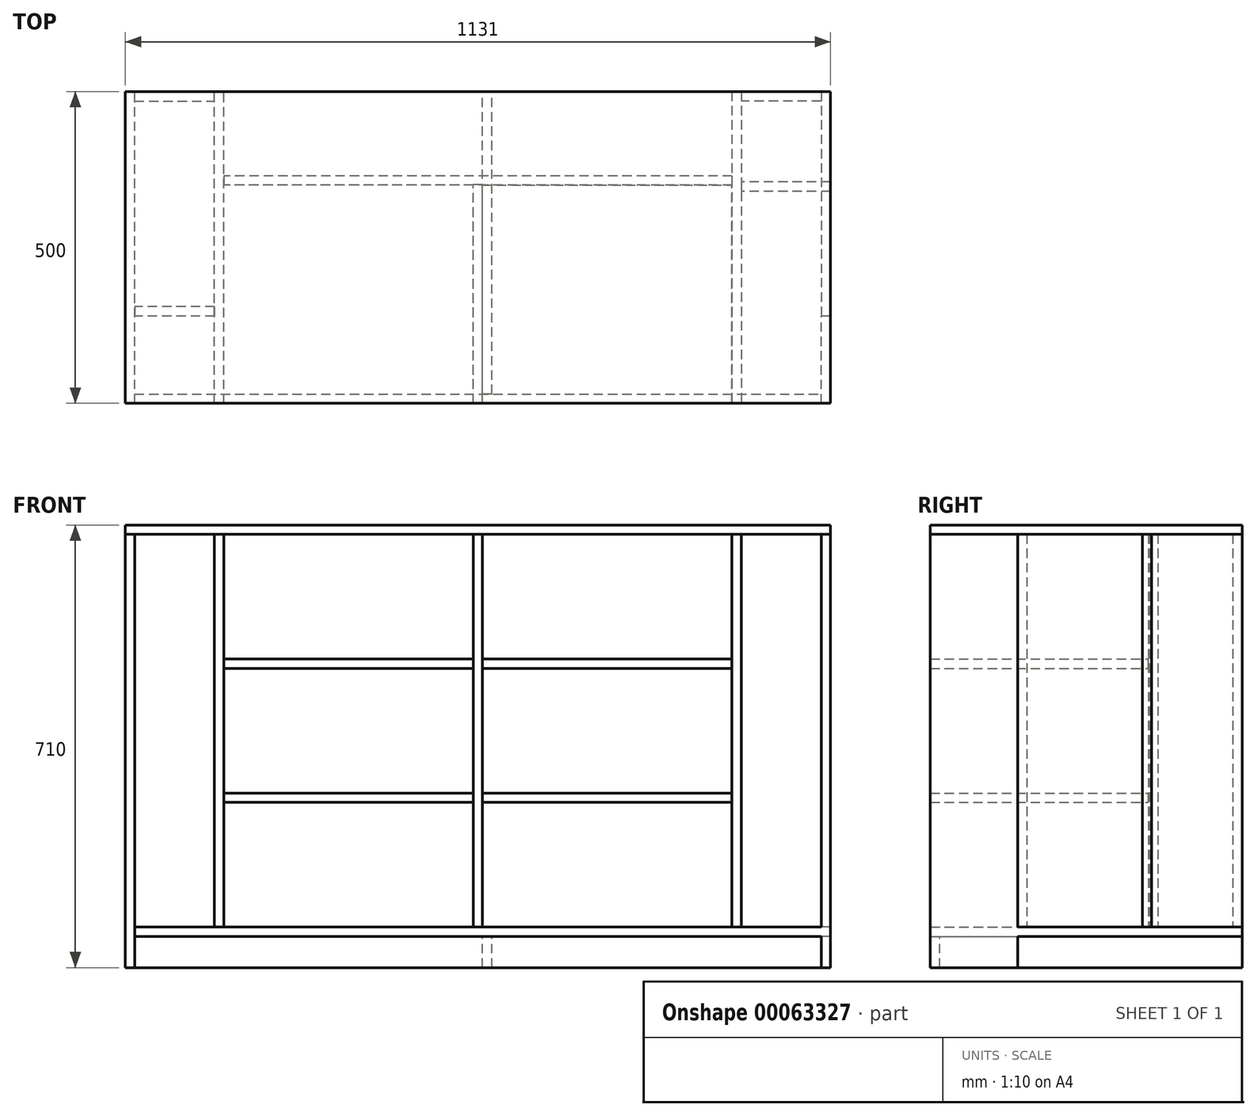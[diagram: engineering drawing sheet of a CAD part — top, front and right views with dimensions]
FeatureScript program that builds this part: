
annotation { "Feature Type Name" : "Feature", "Feature Type Description" : "" }
export const myFeature = defineFeature(function(context is Context, id is Id, definition is map)
    precondition{}
    {
        {
            var Q0;
            Q0=qCreatedBy(makeId("Right.planeOp"),FACE);
            var sketch = newSketch(context, id + "F0", { "sketchPlane" : qUnion([Q0])});
            skLineSegment(sketch, "E0.bottom", {"start": v(0, 0) * mm, "end": v(-500, 0) * mm});
            skLineSegment(sketch, "E0.top", {"start": v(0, 695) * mm, "end": v(-500, 695) * mm});
            skLineSegment(sketch, "E0.left", {"start": v(0, 0) * mm, "end": v(0, 695) * mm});
            skLineSegment(sketch, "E0.right", {"start": v(-500, 0) * mm, "end": v(-500, 695) * mm});
            skSolve(sketch);
        }
        {
            var Q0;
            Q0 = qSketchRegion(id + "F0", true);
            extrude(context, id + "F1", {"entities" : qUnion([Q0]), "depth" : 15 * mm});
        }
        {
            var Q0;
            Q0=makeQuery(id+"F1.opExtrude","SWEPT_FACE",FACE,{"disambiguationData":[OSD([sQuery(id+"F0.wireOp",EDGE,"E0.top")])]});
            var sketch = newSketch(context, id + "F2", { "sketchPlane" : qUnion([Q0])});
            skLineSegment(sketch, "E1.bottom", {"start": v(0, 0) * mm, "end": v(1131, 0) * mm});
            skLineSegment(sketch, "E1.top", {"start": v(0, -500) * mm, "end": v(1131, -500) * mm});
            skLineSegment(sketch, "E1.left", {"start": v(0, 0) * mm, "end": v(0, -500) * mm});
            skLineSegment(sketch, "E1.right", {"start": v(1131, 0) * mm, "end": v(1131, -500) * mm});
            skSolve(sketch);
        }
        {
            var Q0;
            Q0 = qSketchRegion(id + "F2", true);
            extrude(context, id + "F3", {"entities" : qUnion([Q0]), "depth" : 15 * mm});
        }
        {
            var Q0;
            Q0=makeQuery(id+"F1.opExtrude","CAP_FACE",FACE,{"disambiguationData":[OSD([sQuery(id+"F0.wireOp",EDGE,"E0.bottom"),sQuery(id+"F0.wireOp",EDGE,"E0.top"),sQuery(id+"F0.wireOp",EDGE,"E0.left"),sQuery(id+"F0.wireOp",EDGE,"E0.right")])],"isStart":false});
            var sketch = newSketch(context, id + "F4", { "sketchPlane" : qUnion([Q0])});
            skLineSegment(sketch, "E2.bottom", {"start": v(-500, 65) * mm, "end": v(0, 65) * mm});
            skLineSegment(sketch, "E2.top", {"start": v(-500, 50) * mm, "end": v(0, 50) * mm});
            skLineSegment(sketch, "E2.left", {"start": v(-500, 65) * mm, "end": v(-500, 50) * mm});
            skLineSegment(sketch, "E2.right", {"start": v(0, 65) * mm, "end": v(0, 50) * mm});
            skSolve(sketch);
        }
        {
            var Q0;
            Q0 = qSketchRegion(id + "F4", true);
            extrude(context, id + "F5", {"entities" : qUnion([Q0]), "depth" : 1101 * mm});
        }
        {
            var Q0;
            Q0=makeQuery(id+"F5.opExtrude","SWEPT_FACE",FACE,{"disambiguationData":[OSD([sQuery(id+"F4.wireOp",EDGE,"E2.top")])]});
            var sketch = newSketch(context, id + "F6", { "sketchPlane" : qUnion([Q0])});
            skLineSegment(sketch, "E3.bottom", {"start": v(588, 485) * mm, "end": v(573, 485) * mm});
            skLineSegment(sketch, "E3.top", {"start": v(588, 0) * mm, "end": v(573, 0) * mm});
            skLineSegment(sketch, "E3.left", {"start": v(588, 485) * mm, "end": v(588, 0) * mm});
            skLineSegment(sketch, "E3.right", {"start": v(573, 485) * mm, "end": v(573, 0) * mm});
            skSolve(sketch);
        }
        {
            var Q0;
            Q0 = qSketchRegion(id + "F6", true);
            extrude(context, id + "F7", {"entities" : qUnion([Q0]), "depth" : 50 * mm});
        }
        {
            var Q0;
            Q0=makeQuery(id+"F7.opExtrude","SWEPT_FACE",FACE,{"disambiguationData":[OSD([sQuery(id+"F6.wireOp",EDGE,"E3.bottom")])]});
            var sketch = newSketch(context, id + "F8", { "sketchPlane" : qUnion([Q0])});
            skLineSegment(sketch, "E4.bottom", {"start": v(15, 0) * mm, "end": v(1116, 0) * mm});
            skLineSegment(sketch, "E4.top", {"start": v(15, 50) * mm, "end": v(1116, 50) * mm});
            skLineSegment(sketch, "E4.left", {"start": v(15, 0) * mm, "end": v(15, 50) * mm});
            skLineSegment(sketch, "E4.right", {"start": v(1116, 0) * mm, "end": v(1116, 50) * mm});
            skSolve(sketch);
        }
        {
            var Q0;
            Q0 = qSketchRegion(id + "F8", true);
            extrude(context, id + "F9", {"entities" : qUnion([Q0]), "depth" : 15 * mm});
        }
        {
            var Q0;
            Q0=makeQuery(id+"F9.opExtrude","SWEPT_FACE",FACE,{"disambiguationData":[OSD([sQuery(id+"F8.wireOp",EDGE,"E4.right")])]});
            var sketch = newSketch(context, id + "F10", { "sketchPlane" : qUnion([Q0])});
            skLineSegment(sketch, "E5.bottom", {"start": v(-500, 0) * mm, "end": v(-360, 0) * mm});
            skLineSegment(sketch, "E5.top", {"start": v(-500, 695) * mm, "end": v(-360, 695) * mm});
            skLineSegment(sketch, "E5.left", {"start": v(-500, 0) * mm, "end": v(-500, 695) * mm});
            skLineSegment(sketch, "E5.right", {"start": v(-360, 0) * mm, "end": v(-360, 695) * mm});
            skSolve(sketch);
        }
        {
            var Q0;
            Q0 = qSketchRegion(id + "F10", true);
            extrude(context, id + "F11", {"entities" : qUnion([Q0]), "depth" : 15 * mm});
        }
        {
            var Q0;
            Q0=makeQuery(id+"F5.opExtrude","CAP_FACE",FACE,{"disambiguationData":[OSD([sQuery(id+"F4.wireOp",EDGE,"E2.bottom"),sQuery(id+"F4.wireOp",EDGE,"E2.top"),sQuery(id+"F4.wireOp",EDGE,"E2.left"),sQuery(id+"F4.wireOp",EDGE,"E2.right")])],"isStart":false});
            var sketch = newSketch(context, id + "F12", { "sketchPlane" : qUnion([Q0])});
            skLineSegment(sketch, "E6.bottom", {"start": v(0, 65) * mm, "end": v(-360, 65) * mm});
            skLineSegment(sketch, "E6.top", {"start": v(0, 50) * mm, "end": v(-360, 50) * mm});
            skLineSegment(sketch, "E6.left", {"start": v(0, 65) * mm, "end": v(0, 50) * mm});
            skLineSegment(sketch, "E6.right", {"start": v(-360, 65) * mm, "end": v(-360, 50) * mm});
            skSolve(sketch);
        }
        {
            var Q0;
            Q0 = qSketchRegion(id + "F12", true);
            extrude(context, id + "F13", {"entities" : qUnion([Q0]), "operationType" : NewBodyOperationType.ADD, "depth" : 15 * mm});
        }
        {
            var Q0;
            Q0=makeQuery(id+"F13.boolean.opBoolean","MERGE",FACE,{"derivedFrom":[makeQuery(id+"F5.opExtrude","SWEPT_FACE",FACE,{"disambiguationData":[OSD([sQuery(id+"F4.wireOp",EDGE,"E2.top")])]}),makeQuery(id+"F13.opExtrude","SWEPT_FACE",FACE,{"disambiguationData":[OSD([sQuery(id+"F12.wireOp",EDGE,"E6.top")])]})]});
            var sketch = newSketch(context, id + "F14", { "sketchPlane" : qUnion([Q0])});
            skLineSegment(sketch, "E7.bottom", {"start": v(1116, 0) * mm, "end": v(1131, 0) * mm});
            skLineSegment(sketch, "E7.top", {"start": v(1116, 360) * mm, "end": v(1131, 360) * mm});
            skLineSegment(sketch, "E7.left", {"start": v(1116, 0) * mm, "end": v(1116, 360) * mm});
            skLineSegment(sketch, "E7.right", {"start": v(1131, 0) * mm, "end": v(1131, 360) * mm});
            skSolve(sketch);
        }
        {
            var Q0;
            Q0 = qSketchRegion(id + "F14", true);
            extrude(context, id + "F15", {"entities" : qUnion([Q0]), "depth" : 50 * mm});
        }
        {
            var Q0;
            Q0=makeQuery(id+"F3.opExtrude","CAP_FACE",FACE,{"disambiguationData":[OSD([sQuery(id+"F2.wireOp",EDGE,"E1.bottom"),sQuery(id+"F2.wireOp",EDGE,"E1.top"),sQuery(id+"F2.wireOp",EDGE,"E1.left"),sQuery(id+"F2.wireOp",EDGE,"E1.right")])],"isStart":true});
            var sketch = newSketch(context, id + "F16", { "sketchPlane" : qUnion([Q0])});
            skLineSegment(sketch, "E8.bottom", {"start": v(143, 500) * mm, "end": v(158, 500) * mm});
            skLineSegment(sketch, "E8.top", {"start": v(143, 0) * mm, "end": v(158, 0) * mm});
            skLineSegment(sketch, "E8.left", {"start": v(143, 500) * mm, "end": v(143, 0) * mm});
            skLineSegment(sketch, "E8.right", {"start": v(158, 500) * mm, "end": v(158, 0) * mm});
            skSolve(sketch);
        }
        {
            var Q0;
            Q0 = qSketchRegion(id + "F16", true);
            extrude(context, id + "F17", {"entities" : qUnion([Q0]), "depth" : 630 * mm});
        }
        {
            var Q0;
            Q0=makeQuery(id+"F17.opExtrude","SWEPT_FACE",FACE,{"disambiguationData":[OSD([sQuery(id+"F16.wireOp",EDGE,"E8.right")])]});
            var sketch = newSketch(context, id + "F18", { "sketchPlane" : qUnion([Q0])});
            skLineSegment(sketch, "E9.bottom", {"start": v(-500, 480) * mm, "end": v(-150, 480) * mm});
            skLineSegment(sketch, "E9.top", {"start": v(-500, 495) * mm, "end": v(-150, 495) * mm});
            skLineSegment(sketch, "E9.left", {"start": v(-500, 480) * mm, "end": v(-500, 495) * mm});
            skLineSegment(sketch, "E9.right", {"start": v(-150, 480) * mm, "end": v(-150, 495) * mm});
            skSolve(sketch);
        }
        {
            var Q0;
            Q0 = qSketchRegion(id + "F18", true);
            extrude(context, id + "F19", {"entities" : qUnion([Q0]), "depth" : 400 * mm});
        }
        {
            var Q0;
            Q0=makeQuery(id+"F17.opExtrude","SWEPT_FACE",FACE,{"disambiguationData":[OSD([sQuery(id+"F16.wireOp",EDGE,"E8.right")])]});
            var sketch = newSketch(context, id + "F20", { "sketchPlane" : qUnion([Q0])});
            skLineSegment(sketch, "E10.bottom", {"start": v(-500, 265) * mm, "end": v(-150, 265) * mm});
            skLineSegment(sketch, "E10.top", {"start": v(-500, 280) * mm, "end": v(-150, 280) * mm});
            skLineSegment(sketch, "E10.left", {"start": v(-500, 265) * mm, "end": v(-500, 280) * mm});
            skLineSegment(sketch, "E10.right", {"start": v(-150, 265) * mm, "end": v(-150, 280) * mm});
            skSolve(sketch);
        }
        {
            var Q0;
            Q0 = qSketchRegion(id + "F20", true);
            extrude(context, id + "F21", {"entities" : qUnion([Q0]), "depth" : 400 * mm});
        }
        {
            var Q0;
            Q0=makeQuery(id+"F19.opExtrude","SWEPT_FACE",FACE,{"disambiguationData":[OSD([sQuery(id+"F18.wireOp",EDGE,"E9.right")])]});
            var sketch = newSketch(context, id + "F22", { "sketchPlane" : qUnion([Q0])});
            skLineSegment(sketch, "E11.bottom", {"start": v(-973, 695) * mm, "end": v(-158, 695) * mm});
            skLineSegment(sketch, "E11.top", {"start": v(-973, 65) * mm, "end": v(-158, 65) * mm});
            skLineSegment(sketch, "E11.left", {"start": v(-973, 695) * mm, "end": v(-973, 65) * mm});
            skLineSegment(sketch, "E11.right", {"start": v(-158, 695) * mm, "end": v(-158, 65) * mm});
            skSolve(sketch);
        }
        {
            var Q0;
            Q0 = qSketchRegion(id + "F22", true);
            extrude(context, id + "F23", {"entities" : qUnion([Q0]), "depth" : 15 * mm});
        }
        {
            var Q0;
            Q0=makeQuery(id+"F23.opExtrude","SWEPT_FACE",FACE,{"disambiguationData":[OSD([sQuery(id+"F22.wireOp",EDGE,"E11.left")])]});
            var sketch = newSketch(context, id + "F24", { "sketchPlane" : qUnion([Q0])});
            skLineSegment(sketch, "E12.bottom", {"start": v(0, 695) * mm, "end": v(-500, 695) * mm});
            skLineSegment(sketch, "E12.top", {"start": v(0, 65) * mm, "end": v(-500, 65) * mm});
            skLineSegment(sketch, "E12.left", {"start": v(0, 695) * mm, "end": v(0, 65) * mm});
            skLineSegment(sketch, "E12.right", {"start": v(-500, 695) * mm, "end": v(-500, 65) * mm});
            skSolve(sketch);
        }
        {
            var Q0;
            Q0 = qSketchRegion(id + "F24", true);
            extrude(context, id + "F25", {"entities" : qUnion([Q0]), "depth" : 15 * mm});
        }
        {
            var Q0;
            Q0=makeQuery(id+"F23.opExtrude","CAP_FACE",FACE,{"disambiguationData":[OSD([sQuery(id+"F22.wireOp",EDGE,"E11.bottom"),sQuery(id+"F22.wireOp",EDGE,"E11.top"),sQuery(id+"F22.wireOp",EDGE,"E11.left"),sQuery(id+"F22.wireOp",EDGE,"E11.right")])],"isStart":true});
            var sketch = newSketch(context, id + "F26", { "sketchPlane" : qUnion([Q0])});
            skLineSegment(sketch, "E13.bottom", {"start": v(573, 280) * mm, "end": v(973, 280) * mm});
            skLineSegment(sketch, "E13.top", {"start": v(573, 265) * mm, "end": v(973, 265) * mm});
            skLineSegment(sketch, "E13.left", {"start": v(573, 280) * mm, "end": v(573, 265) * mm});
            skLineSegment(sketch, "E13.right", {"start": v(973, 280) * mm, "end": v(973, 265) * mm});
            skSolve(sketch);
        }
        {
            var Q0;
            Q0 = qSketchRegion(id + "F26", true);
            extrude(context, id + "F27", {"entities" : qUnion([Q0]), "depth" : 350 * mm});
        }
        {
            var Q0;
            Q0=makeQuery(id+"F25.opExtrude","CAP_FACE",FACE,{"disambiguationData":[OSD([sQuery(id+"F24.wireOp",EDGE,"E12.bottom"),sQuery(id+"F24.wireOp",EDGE,"E12.top"),sQuery(id+"F24.wireOp",EDGE,"E12.left"),sQuery(id+"F24.wireOp",EDGE,"E12.right")])],"isStart":true});
            var sketch = newSketch(context, id + "F28", { "sketchPlane" : qUnion([Q0])});
            skSolve(sketch);
        }
        {
            var Q0;
            Q0=makeQuery(id+"F28.imprint","IMPRINT",FACE,{"disambiguationData":[TD([[makeQuery(id+"F28.imprint","IMPRINT",EDGE,{"derivedFrom":makeQuery(id+"F25.opExtrude","CAP_EDGE",EDGE,{"disambiguationData":[OSD([sQuery(id+"F24.wireOp",EDGE,"E12.bottom")])],"isStart":true})}),-1.0]])]});
            var sketch = newSketch(context, id + "F29", { "sketchPlane" : qUnion([Q0])});
            skLineSegment(sketch, "E14.bottom", {"start": v(150, 495) * mm, "end": v(500, 495) * mm});
            skLineSegment(sketch, "E14.top", {"start": v(150, 480) * mm, "end": v(500, 480) * mm});
            skLineSegment(sketch, "E14.left", {"start": v(150, 495) * mm, "end": v(150, 480) * mm});
            skLineSegment(sketch, "E14.right", {"start": v(500, 495) * mm, "end": v(500, 480) * mm});
            skSolve(sketch);
        }
        {
            var Q0;
            Q0 = qSketchRegion(id + "F29", true);
            extrude(context, id + "F30", {"entities" : qUnion([Q0]), "depth" : 400 * mm});
        }
        {
            var Q0;
            Q0=makeQuery(id+"F19.opExtrude","CAP_FACE",FACE,{"disambiguationData":[OSD([sQuery(id+"F18.wireOp",EDGE,"E9.bottom"),sQuery(id+"F18.wireOp",EDGE,"E9.top"),sQuery(id+"F18.wireOp",EDGE,"E9.left"),sQuery(id+"F18.wireOp",EDGE,"E9.right")])],"isStart":false});
            var sketch = newSketch(context, id + "F31", { "sketchPlane" : qUnion([Q0])});
            skLineSegment(sketch, "E15.bottom", {"start": v(-499.25, 695) * mm, "end": v(-149.25, 695) * mm});
            skLineSegment(sketch, "E15.top", {"start": v(-499.25, 65) * mm, "end": v(-149.25, 65) * mm});
            skLineSegment(sketch, "E15.left", {"start": v(-499.25, 695) * mm, "end": v(-499.25, 65) * mm});
            skLineSegment(sketch, "E15.right", {"start": v(-149.25, 695) * mm, "end": v(-149.25, 65) * mm});
            skSolve(sketch);
        }
        {
            var Q0;
            Q0 = qSketchRegion(id + "F31", true);
            extrude(context, id + "F32", {"entities" : qUnion([Q0]), "depth" : 15 * mm});
        }
        {
            var Q0;
            Q0=makeQuery(id+"F25.opExtrude","CAP_FACE",FACE,{"disambiguationData":[OSD([sQuery(id+"F24.wireOp",EDGE,"E12.bottom"),sQuery(id+"F24.wireOp",EDGE,"E12.top"),sQuery(id+"F24.wireOp",EDGE,"E12.left"),sQuery(id+"F24.wireOp",EDGE,"E12.right")])],"isStart":false});
            var sketch = newSketch(context, id + "F33", { "sketchPlane" : qUnion([Q0])});
            skLineSegment(sketch, "E16.bottom", {"start": v(-160, 695) * mm, "end": v(-145, 695) * mm});
            skLineSegment(sketch, "E16.top", {"start": v(-160, 65) * mm, "end": v(-145, 65) * mm});
            skLineSegment(sketch, "E16.left", {"start": v(-160, 695) * mm, "end": v(-160, 65) * mm});
            skLineSegment(sketch, "E16.right", {"start": v(-145, 695) * mm, "end": v(-145, 65) * mm});
            skSolve(sketch);
        }
        {
            var Q0;
            Q0 = qSketchRegion(id + "F33", true);
            extrude(context, id + "F34", {"entities" : qUnion([Q0]), "depth" : 143 * mm});
        }
        {
            var Q0;
            Q0=qCreatedBy(makeId("Front.planeOp"),FACE);
            var sketch = newSketch(context, id + "F35", { "sketchPlane" : qUnion([Q0])});
            skLineSegment(sketch, "E17.bottom", {"start": v(15, 65) * mm, "end": v(143, 65) * mm});
            skLineSegment(sketch, "E17.top", {"start": v(15, 695) * mm, "end": v(143, 695) * mm});
            skLineSegment(sketch, "E17.left", {"start": v(15, 65) * mm, "end": v(15, 695) * mm});
            skLineSegment(sketch, "E17.right", {"start": v(143, 65) * mm, "end": v(143, 695) * mm});
            skSolve(sketch);
        }
        {
            var Q0;
            Q0 = qSketchRegion(id + "F35", true);
            extrude(context, id + "F36", {"entities" : qUnion([Q0]), "depth" : 15 * mm});
        }
        {
            var Q0;
            Q0=makeQuery(id+"F1.opExtrude","CAP_FACE",FACE,{"disambiguationData":[OSD([sQuery(id+"F0.wireOp",EDGE,"E0.bottom"),sQuery(id+"F0.wireOp",EDGE,"E0.top"),sQuery(id+"F0.wireOp",EDGE,"E0.left"),sQuery(id+"F0.wireOp",EDGE,"E0.right")])],"isStart":false});
            var sketch = newSketch(context, id + "F37", { "sketchPlane" : qUnion([Q0])});
            skLineSegment(sketch, "E18.bottom", {"start": v(-360, 695) * mm, "end": v(-345, 695) * mm});
            skLineSegment(sketch, "E18.top", {"start": v(-360, 65) * mm, "end": v(-345, 65) * mm});
            skLineSegment(sketch, "E18.left", {"start": v(-360, 695) * mm, "end": v(-360, 65) * mm});
            skLineSegment(sketch, "E18.right", {"start": v(-345, 695) * mm, "end": v(-345, 65) * mm});
            skSolve(sketch);
        }
        {
            var Q0;
            Q0 = qSketchRegion(id + "F37", true);
            extrude(context, id + "F38", {"entities" : qUnion([Q0]), "depth" : 128 * mm});
        }
        {
            var Q0;
            Q0=makeQuery(id+"F25.opExtrude","CAP_FACE",FACE,{"disambiguationData":[OSD([sQuery(id+"F24.wireOp",EDGE,"E12.bottom"),sQuery(id+"F24.wireOp",EDGE,"E12.top"),sQuery(id+"F24.wireOp",EDGE,"E12.left"),sQuery(id+"F24.wireOp",EDGE,"E12.right")])],"isStart":false});
            var sketch = newSketch(context, id + "F39", { "sketchPlane" : qUnion([Q0])});
            skLineSegment(sketch, "E19.bottom", {"start": v(0, 695) * mm, "end": v(-15, 695) * mm});
            skLineSegment(sketch, "E19.top", {"start": v(0, 65) * mm, "end": v(-15, 65) * mm});
            skLineSegment(sketch, "E19.left", {"start": v(0, 695) * mm, "end": v(0, 65) * mm});
            skLineSegment(sketch, "E19.right", {"start": v(-15, 695) * mm, "end": v(-15, 65) * mm});
            skSolve(sketch);
        }
        {
            var Q0;
            Q0 = qSketchRegion(id + "F39", true);
            extrude(context, id + "F40", {"entities" : qUnion([Q0]), "depth" : 128 * mm});
        }
        {
            var Q0;
            Q0=makeQuery(id+"F34.opExtrude","SWEPT_FACE",FACE,{"disambiguationData":[OSD([sQuery(id+"F33.wireOp",EDGE,"E16.right")])]});
            var sketch = newSketch(context, id + "F41", { "sketchPlane" : qUnion([Q0])});
            skLineSegment(sketch, "E20.bottom", {"start": v(-1131, 695) * mm, "end": v(-1116, 695) * mm});
            skLineSegment(sketch, "E20.top", {"start": v(-1131, 65) * mm, "end": v(-1116, 65) * mm});
            skLineSegment(sketch, "E20.left", {"start": v(-1131, 695) * mm, "end": v(-1131, 65) * mm});
            skLineSegment(sketch, "E20.right", {"start": v(-1116, 695) * mm, "end": v(-1116, 65) * mm});
            skSolve(sketch);
        }
        {
            var Q0;
            Q0 = qSketchRegion(id + "F41", true);
            extrude(context, id + "F42", {"entities" : qUnion([Q0]), "depth" : 145 * mm});
        }
    });
